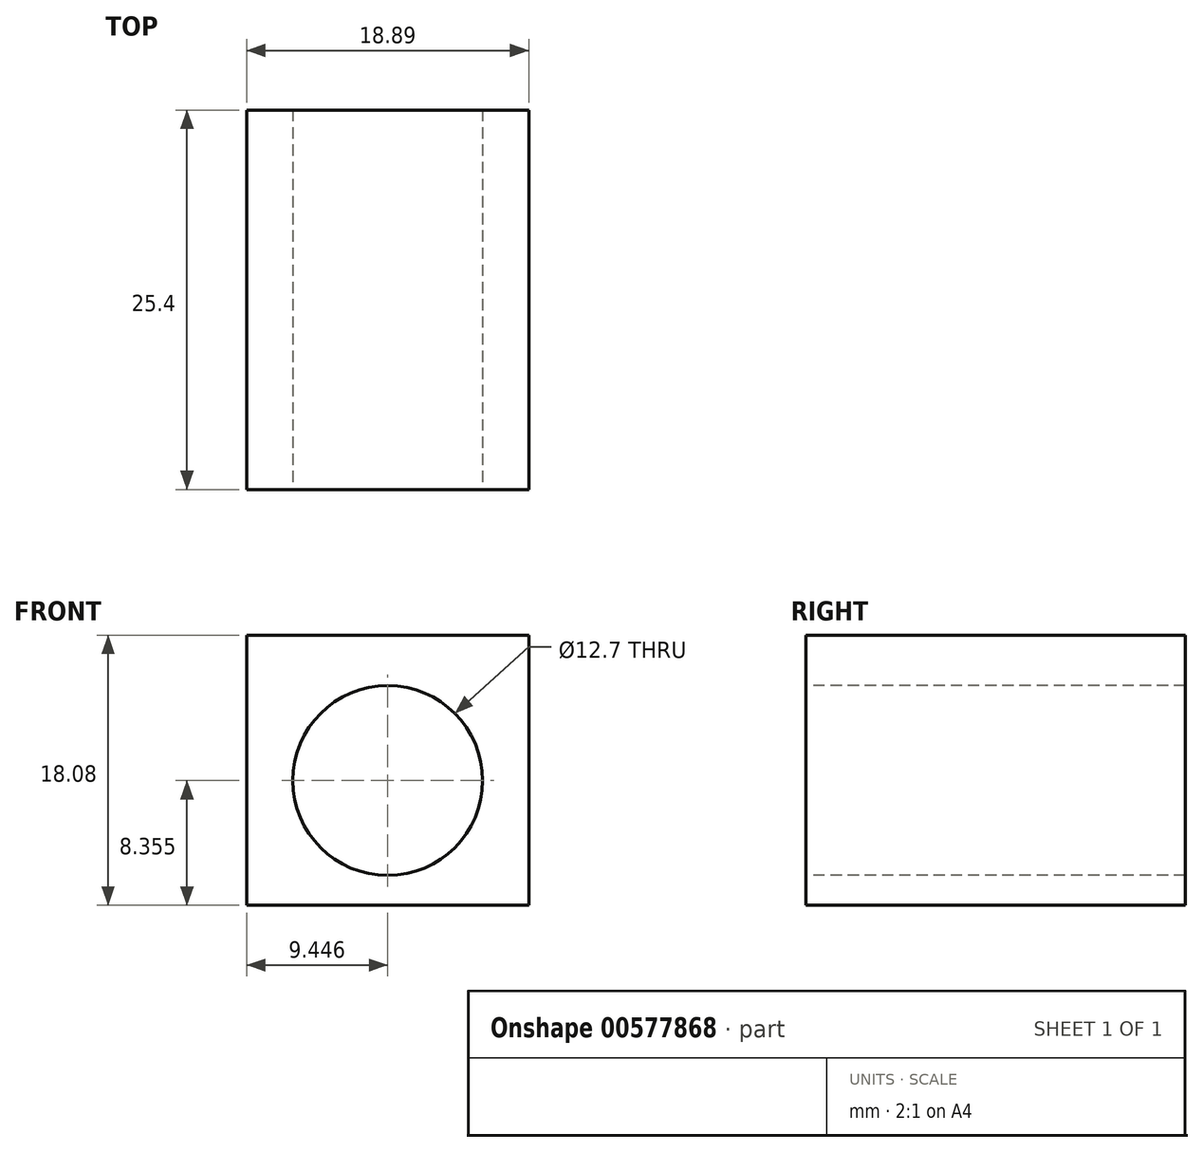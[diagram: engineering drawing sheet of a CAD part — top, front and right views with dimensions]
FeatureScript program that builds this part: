
annotation { "Feature Type Name" : "Feature", "Feature Type Description" : "" }
export const myFeature = defineFeature(function(context is Context, id is Id, definition is map)
    precondition{}
    {
        {
            var Q0;
            Q0=qCreatedBy(makeId("Front.planeOp"),FACE);
            var sketch = newSketch(context, id + "F0", { "sketchPlane" : qUnion([Q0])});
            skLineSegment(sketch, "E0", {"start": v(0, 0) * mm, "end": v(0, -18.08) * mm});
            skLineSegment(sketch, "E1", {"start": v(0, -18.08) * mm, "end": v(18.9, -18.08) * mm});
            skLineSegment(sketch, "E2", {"start": v(18.9, -18.08) * mm, "end": v(18.9, 0) * mm});
            skLineSegment(sketch, "E3", {"start": v(18.9, 0) * mm, "end": v(0, 0) * mm});
            skSolve(sketch);
        }
        {
            var Q0;
            Q0=makeQuery(id+"F0.imprint","IMPRINT",FACE,{"disambiguationData":[TD([[makeQuery(id+"F0.imprint","IMPRINT",EDGE,{"derivedFrom":sQuery(id+"F0.wireOp",EDGE,"E0")}),1.0]])]});
            extrude(context, id + "F1", {"entities" : qUnion([Q0]), "depth" : 25.4 * mm, "offsetDistance" : 25.4 * mm});
        }
        {
            var Q0;
            Q0=makeQuery(id+"F1.opExtrude","CAP_FACE",FACE,{"disambiguationData":[OSD([sQuery(id+"F0.wireOp",EDGE,"E0"),sQuery(id+"F0.wireOp",EDGE,"E1"),sQuery(id+"F0.wireOp",EDGE,"E2"),sQuery(id+"F0.wireOp",EDGE,"E3")])],"isStart":false});
            var sketch = newSketch(context, id + "F2", { "sketchPlane" : qUnion([Q0])});
            skPoint(sketch, "E4", {"position": v(9.45, -9.72) * mm});
            skPoint(sketch, "E4.positionSnap0", {"position": v(9.45, 0) * mm});
            skSolve(sketch);
        }
        {
            var Q0;
            Q0=sQuery(id+"F2.wireOp",VERTEX,"E4");
            var Q1;
            Q1=makeQuery(id+"F1.opExtrude","SWEPT_BODY",BODY,{"disambiguationData":[OSD([sQuery(id+"F0.wireOp",EDGE,"E0"),sQuery(id+"F0.wireOp",EDGE,"E1"),sQuery(id+"F0.wireOp",EDGE,"E2"),sQuery(id+"F0.wireOp",EDGE,"E3")])]});
            hole(context, id + "F3", {"style" : HoleStyle.SIMPLE, "endStyle" : HoleEndStyle.THROUGH, "holeDiameter" : 12.7 * mm, "isTappedThrough" : true, "tappedDepth" : 12.7 * mm, "tapClearance" : 3, "locations" : qUnion([Q0]), "scope" : qUnion([Q1])});
        }
    });
